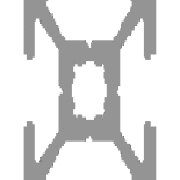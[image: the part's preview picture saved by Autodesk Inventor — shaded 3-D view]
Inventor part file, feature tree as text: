
AUTODESK INVENTOR PART (.ipt)
format: ipt  version: 2021.3 (Build 253353000, 353)  size: 287,232 bytes
history: native  units: mm
features: other x4, sketch x3, extrude x1, plane x1
ambient origin geometry x8: Origin, YZ Plane, XZ Plane, XY Plane, X Axis, Y Axis, Z Axis, Center Point
bodies: Body (feature_tree)
feature tree (9):
  other  "Driven Length"
  other  "Frame Generator"
  extrude  "Extrusion_20x20"  Depth=1.5mm
  other  "Start Plane"
  other  "End Plane"
  sketch  "Sketch"  dims[d7=3.0mm d9=1.5mm d10=0.5mm d13=0.5mm d14=0.5mm d18=3.0mm d19=3.0mm d21=0.5mm d22=0.5mm d23=0.5mm d24=2.75mm d25=1.5mm d26=10.0mm d27=10.0mm d28=3.0mm d29=3.0mm d30=5.5mm d31=1.5mm d32=0.5mm d33=0.5mm d34=0.5mm d35=0.5mm d36=0.5mm d37=0.5mm d38=0.5mm d39=0.5mm d40=0.5mm d41=2.75mm d42=2.75mm d43=0.5mm d44=40.0mm d46=360.0deg d50=-0.0mm d51=200.0mm d52=0.13mm d53=0.0mm d54=90.0deg d55=200.0mm]
  sketch  "Sketch2"  dims[d4=5.5mm d5=1.5mm]
  plane  "Work Plane3"
  sketch  "Sketch3"  dims[d6=1.5mm]
